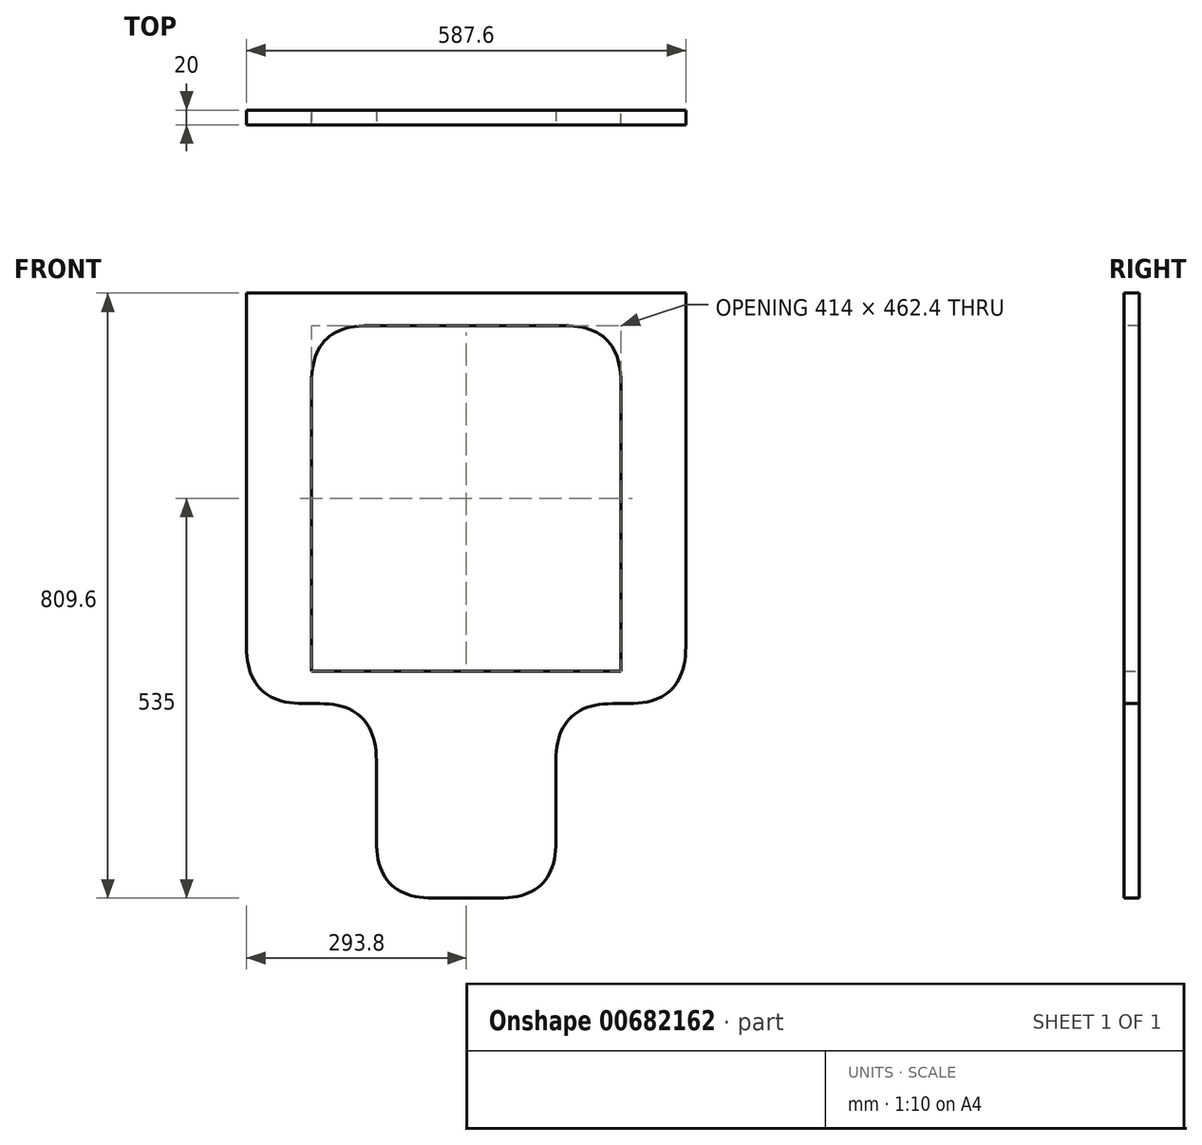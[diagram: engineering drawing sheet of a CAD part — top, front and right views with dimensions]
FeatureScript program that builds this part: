
annotation { "Feature Type Name" : "Feature", "Feature Type Description" : "" }
export const myFeature = defineFeature(function(context is Context, id is Id, definition is map)
    precondition{}
    {
        {
            var Q0;
            Q0=qCreatedBy(makeId("Front.planeOp"),FACE);
            var sketch = newSketch(context, id + "F0", { "sketchPlane" : qUnion([Q0])});
            skLineSegment(sketch, "E0", {"start": v(-293.8, 477) * mm, "end": v(-293.8, -72.2) * mm});
            skLineSegment(sketch, "E1", {"start": v(-293.8, -72.2) * mm, "end": v(-120.2, -72.2) * mm});
            skLineSegment(sketch, "E2", {"start": v(-120.2, -72.2) * mm, "end": v(-120.2, -332.6) * mm});
            skLineSegment(sketch, "E3", {"start": v(-120.2, -332.6) * mm, "end": v(120.2, -332.6) * mm});
            skLineSegment(sketch, "E4", {"start": v(120.2, -332.6) * mm, "end": v(120.2, -72.2) * mm});
            skLineSegment(sketch, "E5", {"start": v(120.2, -72.2) * mm, "end": v(293.8, -72.2) * mm});
            skLineSegment(sketch, "E6", {"start": v(293.8, -72.2) * mm, "end": v(293.8, 477) * mm});
            skLineSegment(sketch, "E7", {"start": v(293.8, 477) * mm, "end": v(-293.8, 477) * mm});
            skSolve(sketch);
        }
        {
            var Q0;
            Q0=makeQuery(id+"F0.imprint","IMPRINT",FACE,{"disambiguationData":[TD([[makeQuery(id+"F0.imprint","IMPRINT",EDGE,{"derivedFrom":sQuery(id+"F0.wireOp",EDGE,"E0")}),1.0]])]});
            var Q1;
            Q1=sQuery(id+"F0.wireOp",EDGE,"E0");
            var Q2;
            Q2=sQuery(id+"F0.wireOp",EDGE,"E1");
            var Q3;
            Q3=sQuery(id+"F0.wireOp",EDGE,"E2");
            var Q4;
            Q4=sQuery(id+"F0.wireOp",EDGE,"E3");
            var Q5;
            Q5=sQuery(id+"F0.wireOp",EDGE,"E4");
            var Q6;
            Q6=sQuery(id+"F0.wireOp",EDGE,"E5");
            var Q7;
            Q7=sQuery(id+"F0.wireOp",EDGE,"E6");
            var Q8;
            Q8=sQuery(id+"F0.wireOp",EDGE,"E7");
            extrude(context, id + "F1", {"entities" : qUnion([Q0]), "surfaceEntities" : qUnion([Q1, Q2, Q3, Q4, Q5, Q6, Q7, Q8]), "depth" : 20 * mm, "offsetDistance" : 25.4 * mm});
        }
        {
            var Q0;
            Q0=makeQuery(id+"F1.opExtrude","SWEPT_EDGE",EDGE,{"disambiguationData":[OSD([sQuery(id+"F0.wireOp",EDGE,"E0"),sQuery(id+"F0.wireOp",EDGE,"E1")])]});
            var Q1;
            Q1=makeQuery(id+"F1.opExtrude","SWEPT_EDGE",EDGE,{"disambiguationData":[OSD([sQuery(id+"F0.wireOp",EDGE,"E1"),sQuery(id+"F0.wireOp",EDGE,"E2")])]});
            var Q2;
            Q2=makeQuery(id+"F1.opExtrude","SWEPT_EDGE",EDGE,{"disambiguationData":[OSD([sQuery(id+"F0.wireOp",EDGE,"E3"),sQuery(id+"F0.wireOp",EDGE,"E4")])]});
            var Q3;
            Q3=makeQuery(id+"F1.opExtrude","SWEPT_EDGE",EDGE,{"disambiguationData":[OSD([sQuery(id+"F0.wireOp",EDGE,"E4"),sQuery(id+"F0.wireOp",EDGE,"E5")])]});
            var Q4;
            Q4=makeQuery(id+"F1.opExtrude","SWEPT_EDGE",EDGE,{"disambiguationData":[OSD([sQuery(id+"F0.wireOp",EDGE,"E5"),sQuery(id+"F0.wireOp",EDGE,"E6")])]});
            var Q5;
            Q5=makeQuery(id+"F1.opExtrude","SWEPT_EDGE",EDGE,{"disambiguationData":[OSD([sQuery(id+"F0.wireOp",EDGE,"E2"),sQuery(id+"F0.wireOp",EDGE,"E3")])]});
            fillet(context, id + "F2", {"entities" : qUnion([Q0, Q1, Q2, Q3, Q4, Q5]), "radius" : 76.2 * mm, "tangentPropagation" : true, "rho" : 0.5, "crossSection" : FilletCrossSection.CONIC, "allowEdgeOverflow" : false});
        }
        {
            var Q0;
            Q0=qCreatedBy(makeId("Front.planeOp"),FACE);
            var sketch = newSketch(context, id + "F3", { "sketchPlane" : qUnion([Q0])});
            skLineSegment(sketch, "E8.bottom", {"start": v(-207, 433.6) * mm, "end": v(207, 433.6) * mm});
            skLineSegment(sketch, "E8.top", {"start": v(-207, -28.8) * mm, "end": v(207, -28.8) * mm});
            skLineSegment(sketch, "E8.left", {"start": v(-207, 433.6) * mm, "end": v(-207, -28.8) * mm});
            skLineSegment(sketch, "E8.right", {"start": v(207, 433.6) * mm, "end": v(207, -28.8) * mm});
            skSolve(sketch);
        }
        {
            var Q0;
            Q0 = qSketchRegion(id + "F3", true);
            extrude(context, id + "F4", {"entities" : qUnion([Q0]), "operationType" : NewBodyOperationType.REMOVE, "depth" : 25.4 * mm, "offsetDistance" : 25.4 * mm});
        }
        {
            var Q0;
            Q0=makeQuery(id+"F4.boolean.opBoolean","COPY",EDGE,{"derivedFrom":makeQuery(id+"F4.opExtrude","SWEPT_EDGE",EDGE,{"disambiguationData":[OSD([sQuery(id+"F3.wireOp",EDGE,"E8.bottom"),sQuery(id+"F3.wireOp",EDGE,"E8.left")])]})});
            var Q1;
            Q1=makeQuery(id+"F4.boolean.opBoolean","COPY",EDGE,{"derivedFrom":makeQuery(id+"F4.opExtrude","SWEPT_EDGE",EDGE,{"disambiguationData":[OSD([sQuery(id+"F3.wireOp",EDGE,"E8.bottom"),sQuery(id+"F3.wireOp",EDGE,"E8.right")])]})});
            fillet(context, id + "F5", {"entities" : qUnion([Q0, Q1]), "radius" : 76.2 * mm, "tangentPropagation" : true, "rho" : 0.5, "crossSection" : FilletCrossSection.CONIC, "allowEdgeOverflow" : false});
        }
    });
